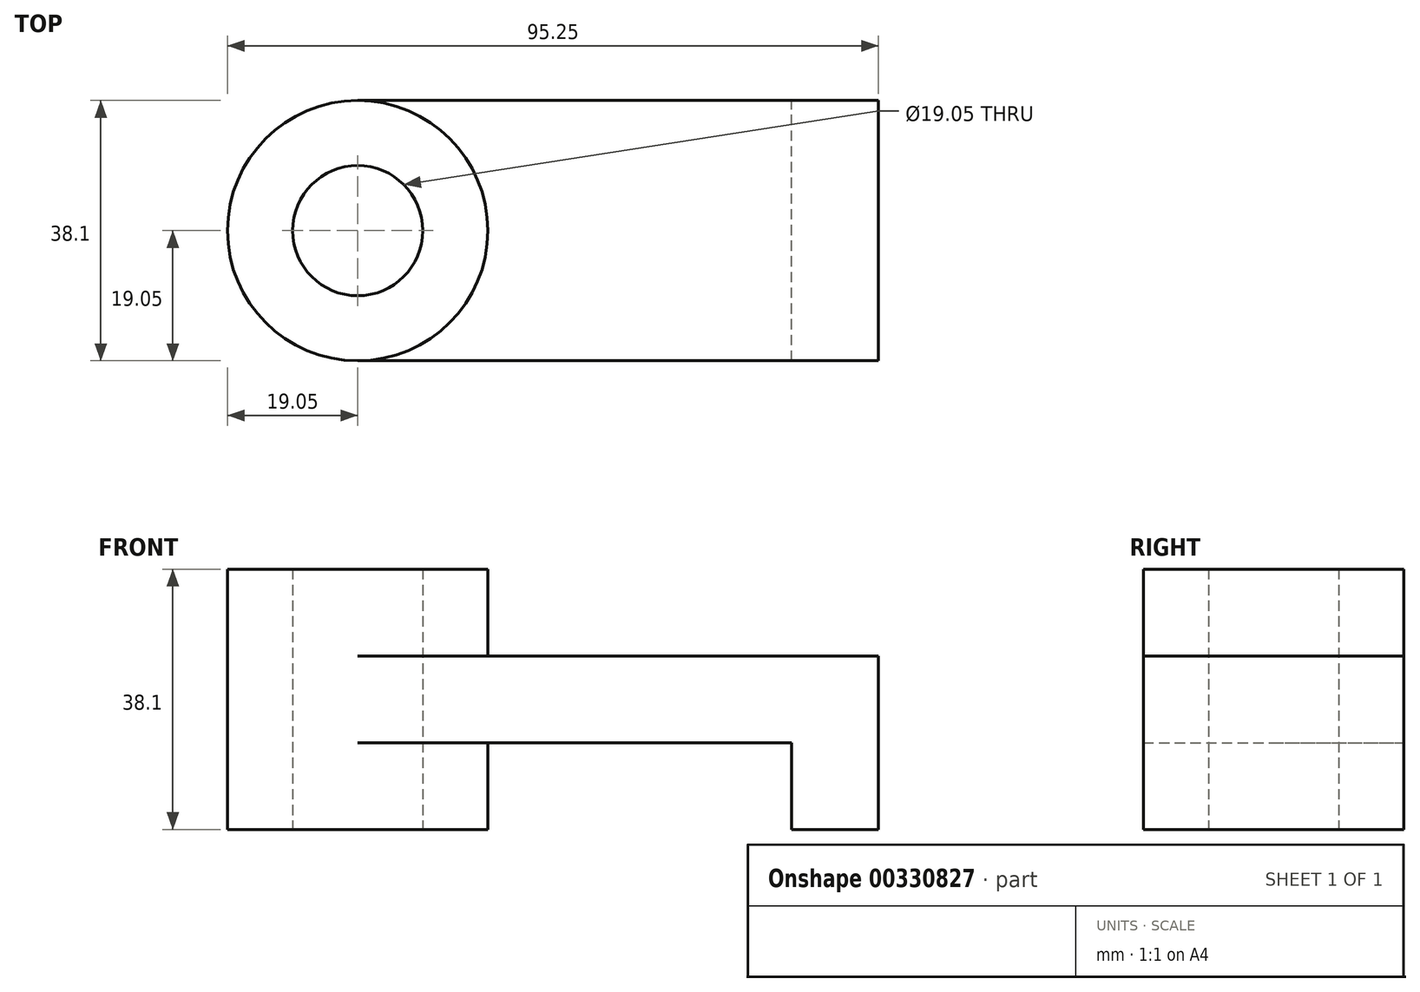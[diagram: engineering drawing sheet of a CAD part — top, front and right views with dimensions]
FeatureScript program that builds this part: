
annotation { "Feature Type Name" : "Feature", "Feature Type Description" : "" }
export const myFeature = defineFeature(function(context is Context, id is Id, definition is map)
    precondition{}
    {
        {
            var Q0;
            Q0=qCreatedBy(makeId("Top.planeOp"),FACE);
            var sketch = newSketch(context, id + "F0", { "sketchPlane" : qUnion([Q0])});
            skPoint(sketch, "E0.middle", {"position": v(0, 0) * mm});
            skLineSegment(sketch, "E1.bottom", {"start": v(38.1, -19.05) * mm, "end": v(-38.1, -19.05) * mm});
            skLineSegment(sketch, "E1.top", {"start": v(38.1, 19.05) * mm, "end": v(-38.1, 19.05) * mm});
            skLineSegment(sketch, "E1.left", {"start": v(38.1, -19.05) * mm, "end": v(38.1, 19.05) * mm});
            skCircle(sketch, "E2", {"center": v(-38.1, 0) * mm, "radius": 19.05 * mm});
            skCircle(sketch, "E3", {"center": v(-38.1, 0) * mm, "radius": 9.53 * mm});
            skSolve(sketch);
        }
        {
            var Q0;
            Q0=makeQuery(id+"F0.imprint","IMPRINT",FACE,{"disambiguationData":[TD([[makeQuery(id+"F0.imprint","IMPRINT",EDGE,{"derivedFrom":sQuery(id+"F0.wireOp",EDGE,"E3")}),-1.0]])]});
            extrude(context, id + "F1", {"entities" : qUnion([Q0]), "endBound" : BoundingType.SYMMETRIC, "depth" : 38.1 * mm});
        }
        {
            var Q0;
            {var subQ0=sQuery(id+"F0.wireOp",EDGE,"E1.bottom");Q0=makeQuery(id+"F0.imprint","IMPRINT",FACE,{"disambiguationData":[TD([[makeQuery(id+"F0.imprint","IMPRINT",EDGE,{"derivedFrom":subQ0}),-1.0]])]});}
            extrude(context, id + "F2", {"entities" : qUnion([Q0]), "operationType" : NewBodyOperationType.ADD, "endBound" : BoundingType.SYMMETRIC, "depth" : 12.7 * mm});
        }
        {
            var Q0;
            Q0=makeQuery(id+"F2.opExtrude","CAP_FACE",FACE,{"disambiguationData":[OSD([sQuery(id+"F0.wireOp",EDGE,"E1.bottom"),sQuery(id+"F0.wireOp",EDGE,"E1.top"),sQuery(id+"F0.wireOp",EDGE,"E1.left"),sQuery(id+"F0.wireOp",EDGE,"E2")])],"isStart":true});
            var sketch = newSketch(context, id + "F3", { "sketchPlane" : qUnion([Q0])});
            skLineSegment(sketch, "E4.bottom", {"start": v(38.1, 19.05) * mm, "end": v(25.4, 19.05) * mm});
            skLineSegment(sketch, "E4.top", {"start": v(38.1, -19.05) * mm, "end": v(25.4, -19.05) * mm});
            skLineSegment(sketch, "E4.left", {"start": v(38.1, 19.05) * mm, "end": v(38.1, -19.05) * mm});
            skLineSegment(sketch, "E4.right", {"start": v(25.4, 19.05) * mm, "end": v(25.4, -19.05) * mm});
            skSolve(sketch);
        }
        {
            var Q0;
            Q0 = qSketchRegion(id + "F3", true);
            extrude(context, id + "F4", {"entities" : qUnion([Q0]), "operationType" : NewBodyOperationType.ADD, "depth" : 12.7 * mm});
        }
    });
